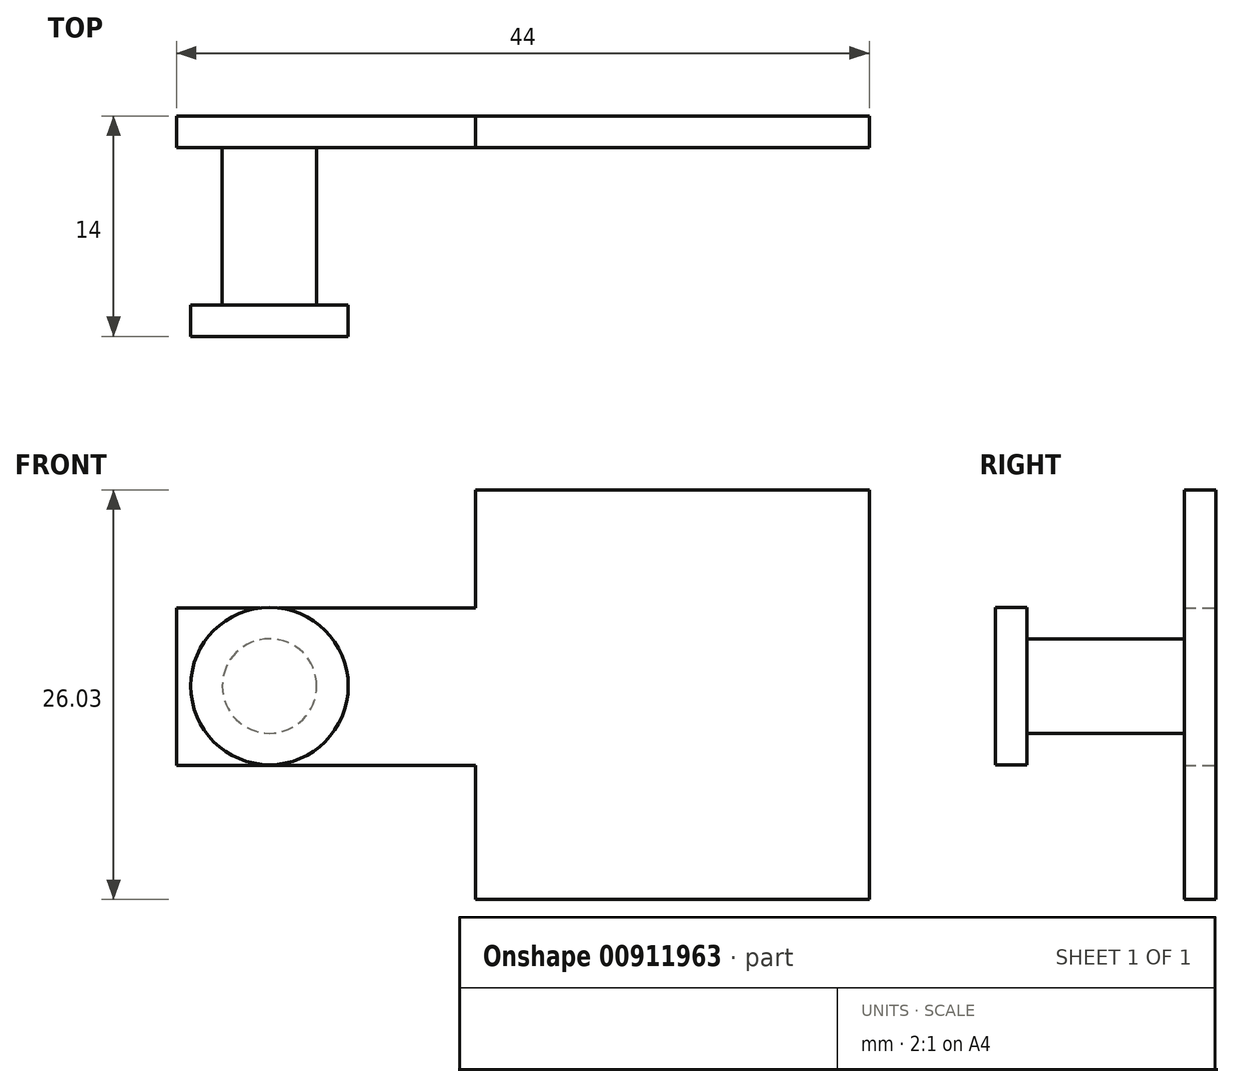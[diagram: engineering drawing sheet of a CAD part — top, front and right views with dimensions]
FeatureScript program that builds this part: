
annotation { "Feature Type Name" : "Feature", "Feature Type Description" : "" }
export const myFeature = defineFeature(function(context is Context, id is Id, definition is map)
    precondition{}
    {
        {
            var Q0;
            Q0=qCreatedBy(makeId("Front.planeOp"),FACE);
            var sketch = newSketch(context, id + "F0", { "sketchPlane" : qUnion([Q0])});
            skLineSegment(sketch, "E0.bottom", {"start": v(-38.12, 30.91) * mm, "end": v(-13.12, 30.91) * mm});
            skLineSegment(sketch, "E0.top", {"start": v(-38.12, 4.88) * mm, "end": v(-13.12, 4.88) * mm});
            skLineSegment(sketch, "E0.left", {"start": v(-38.12, 30.91) * mm, "end": v(-38.12, 23.41) * mm});
            skLineSegment(sketch, "E0.right", {"start": v(-13.12, 30.91) * mm, "end": v(-13.12, 4.88) * mm});
            skLineSegment(sketch, "E1.bottom", {"start": v(-57.12, 23.41) * mm, "end": v(-38.12, 23.41) * mm});
            skLineSegment(sketch, "E1.top", {"start": v(-57.12, 13.41) * mm, "end": v(-38.12, 13.41) * mm});
            skLineSegment(sketch, "E1.left", {"start": v(-57.12, 23.41) * mm, "end": v(-57.12, 13.41) * mm});
            skLineSegment(sketch, "E2.trimOffspring", {"start": v(-38.12, 13.41) * mm, "end": v(-38.12, 4.88) * mm});
            skSolve(sketch);
        }
        {
            var Q0;
            Q0 = qSketchRegion(id + "F0", true);
            extrude(context, id + "F1", {"entities" : qUnion([Q0]), "depth" : 2 * mm, "offsetDistance" : 25 * mm});
        }
        {
            var Q0;
            Q0=makeQuery(id+"F1.opExtrude","CAP_FACE",FACE,{"disambiguationData":[OSD([sQuery(id+"F0.wireOp",EDGE,"E0.bottom"),sQuery(id+"F0.wireOp",EDGE,"E0.top"),sQuery(id+"F0.wireOp",EDGE,"E0.left"),sQuery(id+"F0.wireOp",EDGE,"E0.right"),sQuery(id+"F0.wireOp",EDGE,"E1.bottom"),sQuery(id+"F0.wireOp",EDGE,"E1.top"),sQuery(id+"F0.wireOp",EDGE,"E1.left"),sQuery(id+"F0.wireOp",EDGE,"E2.trimOffspring")])],"isStart":false});
            var sketch = newSketch(context, id + "F2", { "sketchPlane" : qUnion([Q0])});
            skCircle(sketch, "E3", {"center": v(-51.22, 18.44) * mm, "radius": 3 * mm});
            skSolve(sketch);
        }
        {
            var Q0;
            Q0 = qSketchRegion(id + "F2", true);
            extrude(context, id + "F3", {"entities" : qUnion([Q0]), "operationType" : NewBodyOperationType.ADD, "depth" : 10 * mm, "offsetDistance" : 25 * mm});
        }
        {
            var Q0;
            Q0=makeQuery(id+"F3.opExtrude","CAP_FACE",FACE,{"disambiguationData":[OSD([sQuery(id+"F2.wireOp",EDGE,"E3")])],"isStart":false});
            var sketch = newSketch(context, id + "F4", { "sketchPlane" : qUnion([Q0])});
            skCircle(sketch, "E4", {"center": v(-51.22, 18.44) * mm, "radius": 5 * mm});
            skSolve(sketch);
        }
        {
            var Q0;
            Q0 = qSketchRegion(id + "F4", true);
            extrude(context, id + "F5", {"entities" : qUnion([Q0]), "operationType" : NewBodyOperationType.ADD, "depth" : 2 * mm, "offsetDistance" : 25 * mm});
        }
    });
